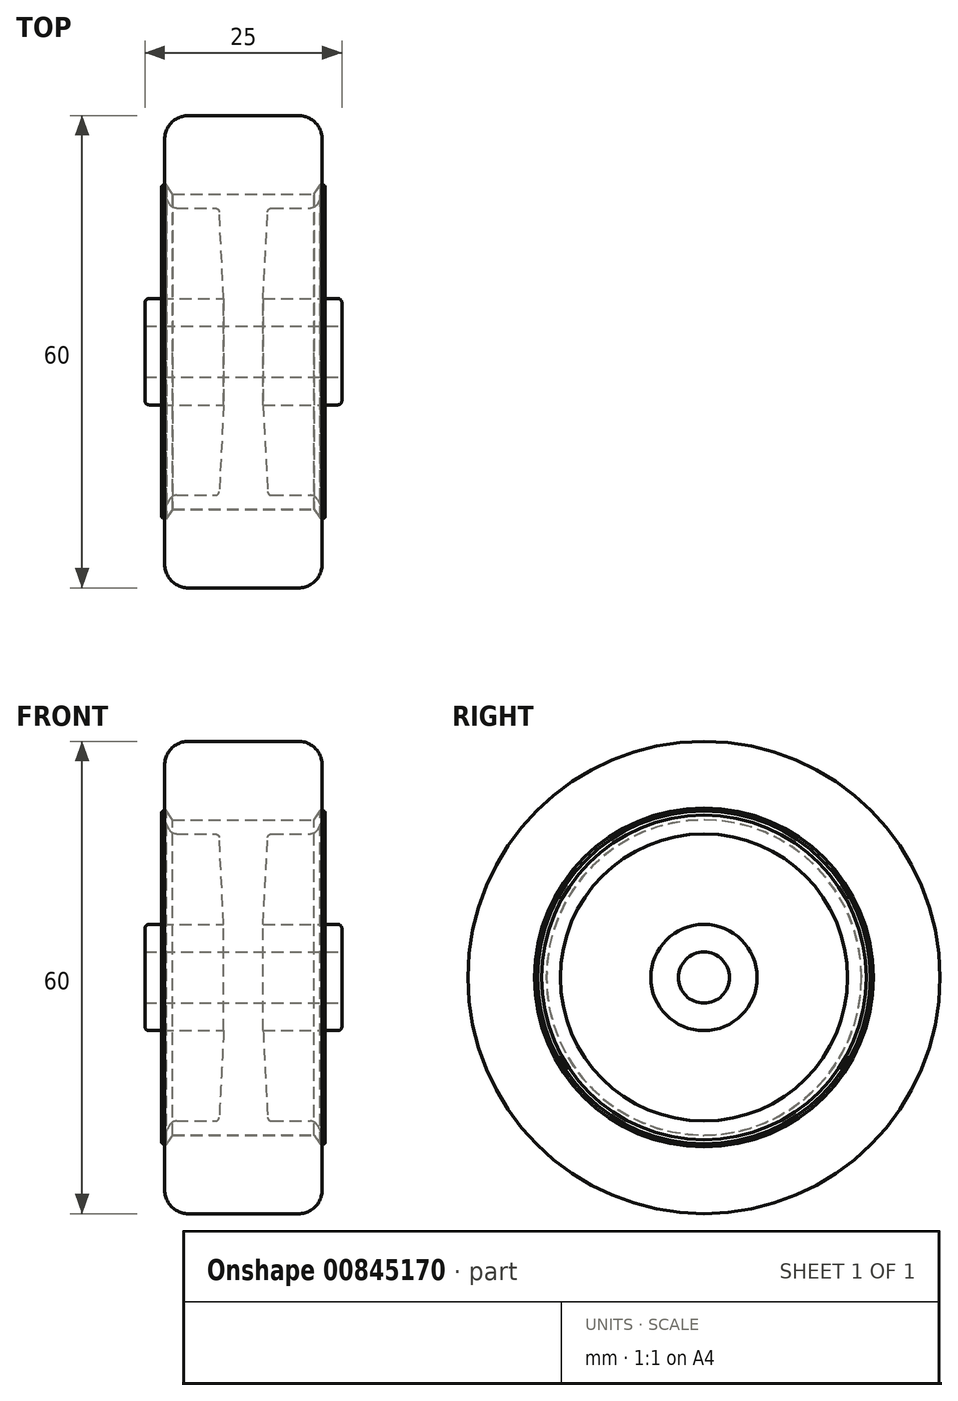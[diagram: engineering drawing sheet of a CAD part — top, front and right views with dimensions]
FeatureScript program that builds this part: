
annotation { "Feature Type Name" : "Feature", "Feature Type Description" : "" }
export const myFeature = defineFeature(function(context is Context, id is Id, definition is map)
    precondition{}
    {
        {
            var Q0;
            Q0=qCreatedBy(makeId("Top.planeOp"),FACE);
            var sketch = newSketch(context, id + "F0", { "sketchPlane" : qUnion([Q0])});
            skLineSegment(sketch, "E0", {"start": v(0, 0) * mm, "end": v(-40.89, 0) * mm, "construction": true});
            skLineSegment(sketch, "E1", {"start": v(0, 0) * mm, "end": v(0, 30) * mm, "construction": true});
            skLineSegment(sketch, "E2", {"start": v(0, 30) * mm, "end": v(-7, 30) * mm});
            skLineSegment(sketch, "E3", {"start": v(0, 3.25) * mm, "end": v(-12.5, 3.25) * mm});
            skLineSegment(sketch, "E4", {"start": v(-12.5, 3.25) * mm, "end": v(-12.5, 6.25) * mm});
            skLineSegment(sketch, "E5", {"start": v(-12, 6.75) * mm, "end": v(-2.5, 6.75) * mm});
            skLineSegment(sketch, "E6", {"start": v(-2.5, 6.75) * mm, "end": v(-3.08, 17.76) * mm});
            skLineSegment(sketch, "E7", {"start": v(0, 20) * mm, "end": v(-9, 20) * mm});
            skLineSegment(sketch, "E8", {"start": v(-9, 20) * mm, "end": v(-9.74, 21.14) * mm});
            skLineSegment(sketch, "E9", {"start": v(-3.58, 18.23) * mm, "end": v(-8.5, 18.23) * mm});
            skLineSegment(sketch, "E10", {"start": v(-9.38, 18.76) * mm, "end": v(-10.38, 20.62) * mm});
            skPoint(sketch, "E11.visualSharp", {"position": v(-9.1, 18.23) * mm});
            skArc(sketch, "E11.filletArc", {"start": v(-9.38, 18.76) * mm, "mid": v(-9.02, 18.38) * mm, "end": v(-8.5, 18.23) * mm});
            skPoint(sketch, "E12.visualSharp", {"position": v(-3.1, 18.23) * mm});
            skArc(sketch, "E12.filletArc", {"start": v(-3.08, 17.76) * mm, "mid": v(-3.23, 18.1) * mm, "end": v(-3.58, 18.23) * mm});
            skLineSegment(sketch, "E13", {"start": v(-9.74, 21.14) * mm, "end": v(-10.18, 21.14) * mm});
            skLineSegment(sketch, "E14", {"start": v(-10.38, 20.94) * mm, "end": v(-10.38, 20.62) * mm});
            skPoint(sketch, "E15.visualSharp", {"position": v(-10.38, 21.14) * mm});
            skArc(sketch, "E15.filletArc", {"start": v(-10.18, 21.14) * mm, "mid": v(-10.33, 21.08) * mm, "end": v(-10.38, 20.94) * mm});
            skLineSegment(sketch, "E16", {"start": v(-10, 27) * mm, "end": v(-10, 21.53) * mm});
            skLineSegment(sketch, "E17", {"start": v(-9, 20) * mm, "end": v(0, 20) * mm});
            skPoint(sketch, "E18.visualSharp", {"position": v(-10, 30) * mm});
            skArc(sketch, "E18.filletArc", {"start": v(-7, 30) * mm, "mid": v(-9.12, 29.12) * mm, "end": v(-10, 27) * mm});
            skLineSegment(sketch, "E19.MirrorCS", {"start": v(0, 30) * mm, "end": v(7, 30) * mm});
            skArc(sketch, "E20.MirrorCS", {"start": v(7, 30) * mm, "mid": v(9.12, 29.12) * mm, "end": v(10, 27) * mm});
            skLineSegment(sketch, "E21.MirrorCS", {"start": v(10, 27) * mm, "end": v(10, 21.53) * mm});
            skLineSegment(sketch, "E22.MirrorCS", {"start": v(9, 20) * mm, "end": v(0, 20) * mm});
            skLineSegment(sketch, "E23.MirrorCS", {"start": v(9.38, 18.76) * mm, "end": v(10.38, 20.62) * mm});
            skLineSegment(sketch, "E24.MirrorCS", {"start": v(9.74, 21.14) * mm, "end": v(10.18, 21.14) * mm});
            skArc(sketch, "E25.MirrorCS", {"start": v(10.18, 21.14) * mm, "mid": v(10.33, 21.08) * mm, "end": v(10.38, 20.94) * mm});
            skLineSegment(sketch, "E26.MirrorCS", {"start": v(10.38, 20.94) * mm, "end": v(10.38, 20.62) * mm});
            skArc(sketch, "E27.MirrorCS", {"start": v(9.38, 18.76) * mm, "mid": v(9.02, 18.38) * mm, "end": v(8.5, 18.23) * mm});
            skLineSegment(sketch, "E28.MirrorCS", {"start": v(3.58, 18.23) * mm, "end": v(8.5, 18.23) * mm});
            skArc(sketch, "E29.MirrorCS", {"start": v(3.08, 17.76) * mm, "mid": v(3.23, 18.1) * mm, "end": v(3.58, 18.23) * mm});
            skLineSegment(sketch, "E30.MirrorCS", {"start": v(2.5, 6.75) * mm, "end": v(3.08, 17.76) * mm});
            skLineSegment(sketch, "E31.MirrorCS", {"start": v(12, 6.75) * mm, "end": v(2.5, 6.75) * mm});
            skLineSegment(sketch, "E32.MirrorCS", {"start": v(12.5, 3.25) * mm, "end": v(12.5, 6.25) * mm});
            skLineSegment(sketch, "E33.MirrorCS", {"start": v(0, 3.25) * mm, "end": v(12.5, 3.25) * mm});
            skPoint(sketch, "E34.visualSharp", {"position": v(-12.5, 6.75) * mm});
            skArc(sketch, "E34.filletArc", {"start": v(-12, 6.75) * mm, "mid": v(-12.35, 6.6) * mm, "end": v(-12.5, 6.25) * mm});
            skPoint(sketch, "E35.visualSharp", {"position": v(12.5, 6.75) * mm});
            skArc(sketch, "E35.filletArc", {"start": v(12.5, 6.25) * mm, "mid": v(12.35, 6.6) * mm, "end": v(12, 6.75) * mm});
            skLineSegment(sketch, "E36", {"start": v(9, 20) * mm, "end": v(9.74, 21.14) * mm});
            skLineSegment(sketch, "E37", {"start": v(-10, 21.53) * mm, "end": v(-9, 20.04) * mm});
            skLineSegment(sketch, "E38", {"start": v(-9, 20.04) * mm, "end": v(0, 20.04) * mm});
            skLineSegment(sketch, "E39.MirrorCS", {"start": v(10, 21.53) * mm, "end": v(9, 20.04) * mm});
            skLineSegment(sketch, "E40.MirrorCS", {"start": v(9, 20.04) * mm, "end": v(0, 20.04) * mm});
            skSolve(sketch);
        }
        {
            var Q0;
            Q0 = qSketchRegion(id + "F0", true);
            var Q1;
            Q1=sQuery(id+"F0.wireOp",EDGE,"E0");
            revolve(context, id + "F1", {"surfaceOperationType" : NewSurfaceOperationType.NEW, "entities" : qUnion([Q0]), "axis" : qUnion([Q1]), "revolveType" : RevolveType.FULL});
        }
    });
